# Revit family: WALL WASHER LIGHTBAR_LKT24WW.15
name_source: partatom
category: Luminarias
units: mm (PartAtom-declared; Revit-internal decimal feet)

## family parameters
Compartido = No
Corte con vacíos al cargar = No
Cota de conector redondo = Diámetro de uso
Origen de luz = Sí
Punto de cálculo de habitación = No
Se basa en plano de trabajo = Sí
Siempre vertical = No
Tipo de pieza = Normal

## types (1)
- REFL_LKT24WW.15
    Archivo de red fotométrica = LKT24WW15.ies
    Cambio de temperatura de color de luz atenuada = Curva de lámpara incandescente
    Comentarios de vataje = 24V
    Descripción = LUMINARIA TIPO REFLECTOR LINEAL, WALL WASHER , CUERPO EN ALUMINIO EXTRUIDO ANODIZADO, CUENTA CON 24 LED TIPO CREE CON UN CONSUMO TOTAL DE 26.4W, 2880 LUMENES, A UNA TEMPERATURA EN BLANCO CALIDO DE 3000K, IP 65, IRC 80, CABLE DE 1M, APERTURA DE 15 GRADOS EN STOCK, ALIMENTADA A 24V. REQUIERE ACCESORIOS.
    Elevación por defecto = 0 mm  [stored 0 ft]
    Fabricante = BRILLANT
    Filtro de color = 16777215
    Longitud de línea de emisión = 400 mm
    Lámpara = CREE
    Modelo = LKT24WW.15
    Watt per fixture = 26.4
    Ángulo de inclinación = 15.00°

note: [stored X ft] marks values corroborated as IEEE doubles in the binary element streams (Revit-internal decimal feet)

## geometry (parser evidence)
native form markers: Blend x2
no freeform markers — native parametric forms only
